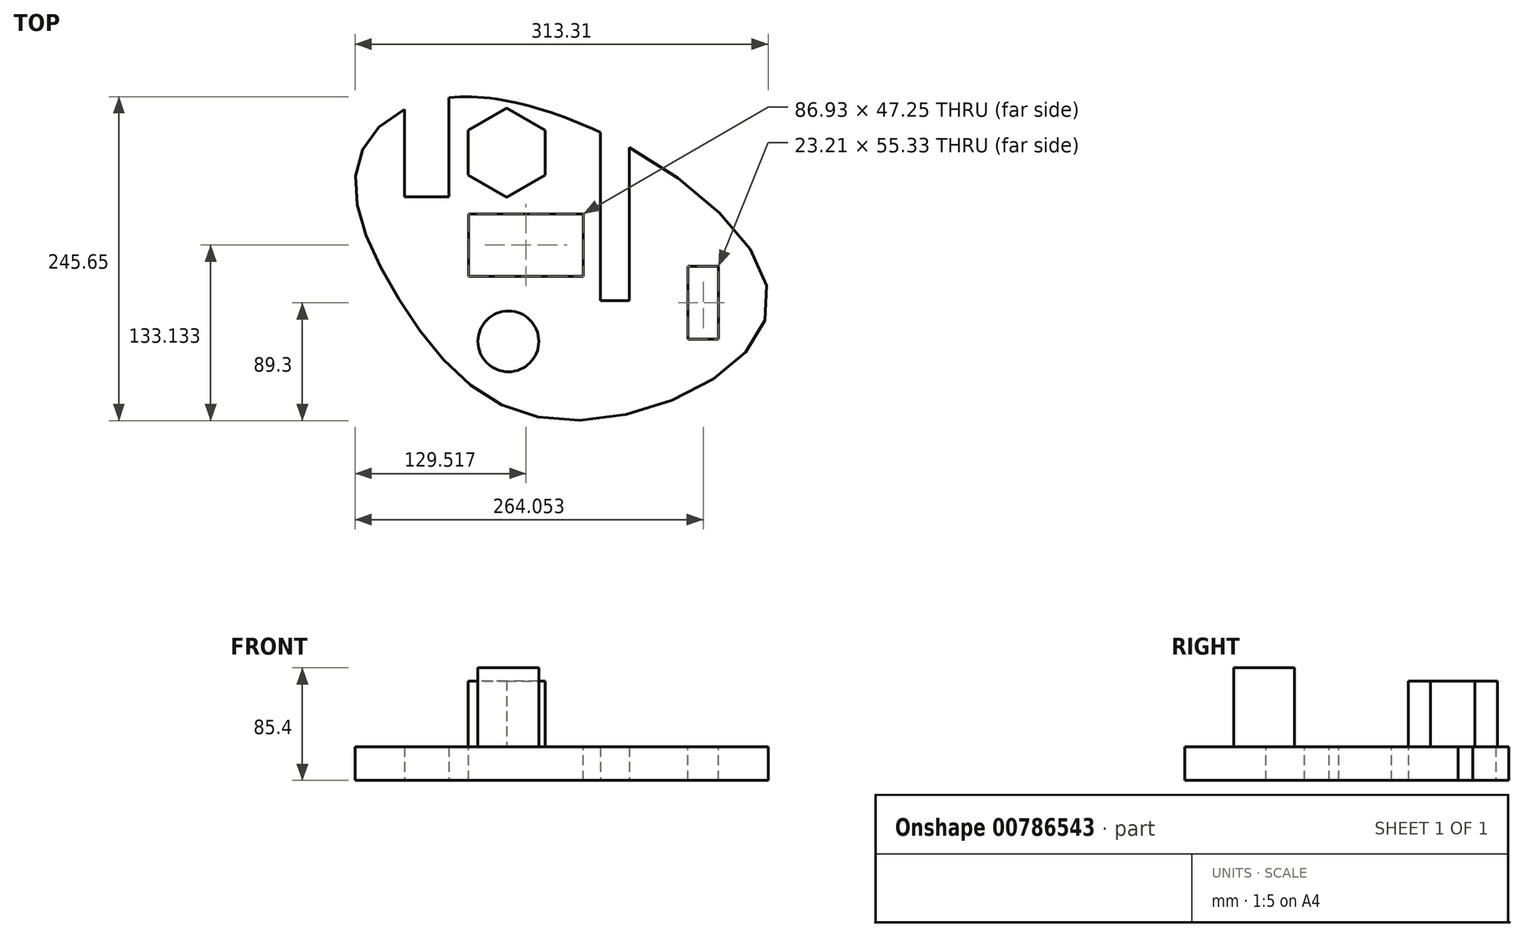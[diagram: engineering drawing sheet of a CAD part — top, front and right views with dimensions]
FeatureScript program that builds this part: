
annotation { "Feature Type Name" : "Feature", "Feature Type Description" : "" }
export const myFeature = defineFeature(function(context is Context, id is Id, definition is map)
    precondition{}
    {
        {
            var Q0;
            Q0=qCreatedBy(makeId("Top.planeOp"),FACE);
            var sketch = newSketch(context, id + "F0", { "sketchPlane" : qUnion([Q0])});
            skFitSpline(sketch, "E0", {"points": [v(-120.42, 0) * mm, v(-152.75, 108.98) * mm, v(-50.04, 154.89) * mm, v(157.82, 0) * mm, v(0, -88.97) * mm, v(-120.42, 0) * mm]});
            skSolve(sketch);
        }
        {
            var Q0;
            Q0=makeQuery(id+"F0.imprint","IMPRINT",FACE,{"disambiguationData":[TD([[makeQuery(id+"F0.imprint","IMPRINT",EDGE,{"derivedFrom":sQuery(id+"F0.wireOp",EDGE,"E0")}),-1.0]])]});
            extrude(context, id + "F1", {"entities" : qUnion([Q0]), "depth" : 25.4 * mm, "offsetDistance" : 25.4 * mm});
        }
        {
            var Q0;
            Q0=makeQuery(id+"F1.opExtrude","CAP_FACE",FACE,{"disambiguationData":[OSD([sQuery(id+"F0.wireOp",EDGE,"E0")])],"isStart":false});
            var sketch = newSketch(context, id + "F2", { "sketchPlane" : qUnion([Q0])});
            skLineSegment(sketch, "E1.bottom", {"start": v(-69.4, 67.46) * mm, "end": v(17.53, 67.46) * mm});
            skLineSegment(sketch, "E1.top", {"start": v(-69.4, 20.2) * mm, "end": v(17.53, 20.2) * mm});
            skLineSegment(sketch, "E1.left", {"start": v(-69.4, 67.46) * mm, "end": v(-69.4, 20.2) * mm});
            skLineSegment(sketch, "E1.right", {"start": v(17.53, 67.46) * mm, "end": v(17.53, 20.2) * mm});
            skPoint(sketch, "E1.middle", {"position": v(-25.93, 43.83) * mm});
            skLineSegment(sketch, "E2.bottom", {"start": v(-84.25, 80.42) * mm, "end": v(-117.9, 80.42) * mm});
            skLineSegment(sketch, "E2.top", {"start": v(-84.25, 161.32) * mm, "end": v(-117.9, 161.32) * mm});
            skLineSegment(sketch, "E2.left", {"start": v(-84.25, 80.42) * mm, "end": v(-84.25, 161.32) * mm});
            skLineSegment(sketch, "E2.right", {"start": v(-117.9, 80.42) * mm, "end": v(-117.9, 161.32) * mm});
            skPoint(sketch, "E2.middle", {"position": v(-101.08, 120.87) * mm});
            skLineSegment(sketch, "E3.bottom", {"start": v(97, 27.67) * mm, "end": v(120.2, 27.67) * mm});
            skLineSegment(sketch, "E3.top", {"start": v(97, -27.67) * mm, "end": v(120.2, -27.67) * mm});
            skLineSegment(sketch, "E3.left", {"start": v(97, 27.67) * mm, "end": v(97, -27.67) * mm});
            skLineSegment(sketch, "E3.right", {"start": v(120.2, 27.67) * mm, "end": v(120.2, -27.67) * mm});
            skPoint(sketch, "E3.middle", {"position": v(108.6, 0) * mm});
            skLineSegment(sketch, "E4.bottom", {"start": v(30.59, 159.27) * mm, "end": v(52.63, 159.27) * mm});
            skLineSegment(sketch, "E4.top", {"start": v(30.59, 1.58) * mm, "end": v(52.63, 1.58) * mm});
            skLineSegment(sketch, "E4.left", {"start": v(30.59, 159.27) * mm, "end": v(30.59, 1.58) * mm});
            skLineSegment(sketch, "E4.right", {"start": v(52.63, 159.27) * mm, "end": v(52.63, 1.58) * mm});
            skPoint(sketch, "E4.middle", {"position": v(41.61, 80.42) * mm});
            skSolve(sketch);
        }
        {
            var Q0;
            Q0 = qSketchRegion(id + "F2", true);
            extrude(context, id + "F3", {"entities" : qUnion([Q0]), "operationType" : NewBodyOperationType.REMOVE, "oppositeDirection" : true, "depth" : 30 * mm, "offsetDistance" : 25 * mm});
        }
        {
            var Q0;
            Q0=makeQuery(id+"F1.opExtrude","CAP_FACE",FACE,{"disambiguationData":[OSD([sQuery(id+"F0.wireOp",EDGE,"E0")])],"isStart":false});
            var sketch = newSketch(context, id + "F4", { "sketchPlane" : qUnion([Q0])});
            skCircle(sketch, "E5", {"center": v(-39.2, -29.2) * mm, "radius": 23.06 * mm});
            skSolve(sketch);
        }
        {
            var Q0;
            Q0=makeQuery(id+"F4.imprint","IMPRINT",FACE,{"disambiguationData":[TD([[makeQuery(id+"F4.imprint","IMPRINT",EDGE,{"derivedFrom":sQuery(id+"F4.wireOp",EDGE,"E5")}),1.0]])]});
            extrude(context, id + "F5", {"entities" : qUnion([Q0]), "operationType" : NewBodyOperationType.ADD, "depth" : 60 * mm, "offsetDistance" : 25 * mm});
        }
        {
            var Q0;
            Q0=makeQuery(id+"F1.opExtrude","CAP_FACE",FACE,{"disambiguationData":[OSD([sQuery(id+"F0.wireOp",EDGE,"E0")])],"isStart":false});
            var sketch = newSketch(context, id + "F6", { "sketchPlane" : qUnion([Q0])});
            skCircle(sketch, "E6.cCircle", {"center": v(-40.52, 113.93) * mm, "radius": 29.3 * mm, "construction": true});
            skLineSegment(sketch, "E6.0", {"start": v(-69.82, 97) * mm, "end": v(-69.82, 130.85) * mm});
            skLineSegment(sketch, "E6.1", {"start": v(-69.82, 130.85) * mm, "end": v(-40.52, 147.77) * mm});
            skLineSegment(sketch, "E6.2", {"start": v(-40.52, 147.77) * mm, "end": v(-11.2, 130.85) * mm});
            skLineSegment(sketch, "E6.3", {"start": v(-11.2, 130.85) * mm, "end": v(-11.2, 97) * mm});
            skLineSegment(sketch, "E6.4", {"start": v(-11.2, 97) * mm, "end": v(-40.52, 80.09) * mm});
            skLineSegment(sketch, "E6.5", {"start": v(-40.52, 80.09) * mm, "end": v(-69.82, 97) * mm});
            skPoint(sketch, "E6.0.midPoint", {"position": v(-69.82, 113.93) * mm});
            skSolve(sketch);
        }
        {
            var Q0;
            Q0=makeQuery(id+"F6.imprint","IMPRINT",FACE,{"disambiguationData":[TD([[makeQuery(id+"F6.imprint","IMPRINT",EDGE,{"derivedFrom":sQuery(id+"F6.wireOp",EDGE,"E6.0")}),-1.0]])]});
            extrude(context, id + "F7", {"entities" : qUnion([Q0]), "operationType" : NewBodyOperationType.ADD, "depth" : 50 * mm, "offsetDistance" : 25 * mm});
        }
    });
